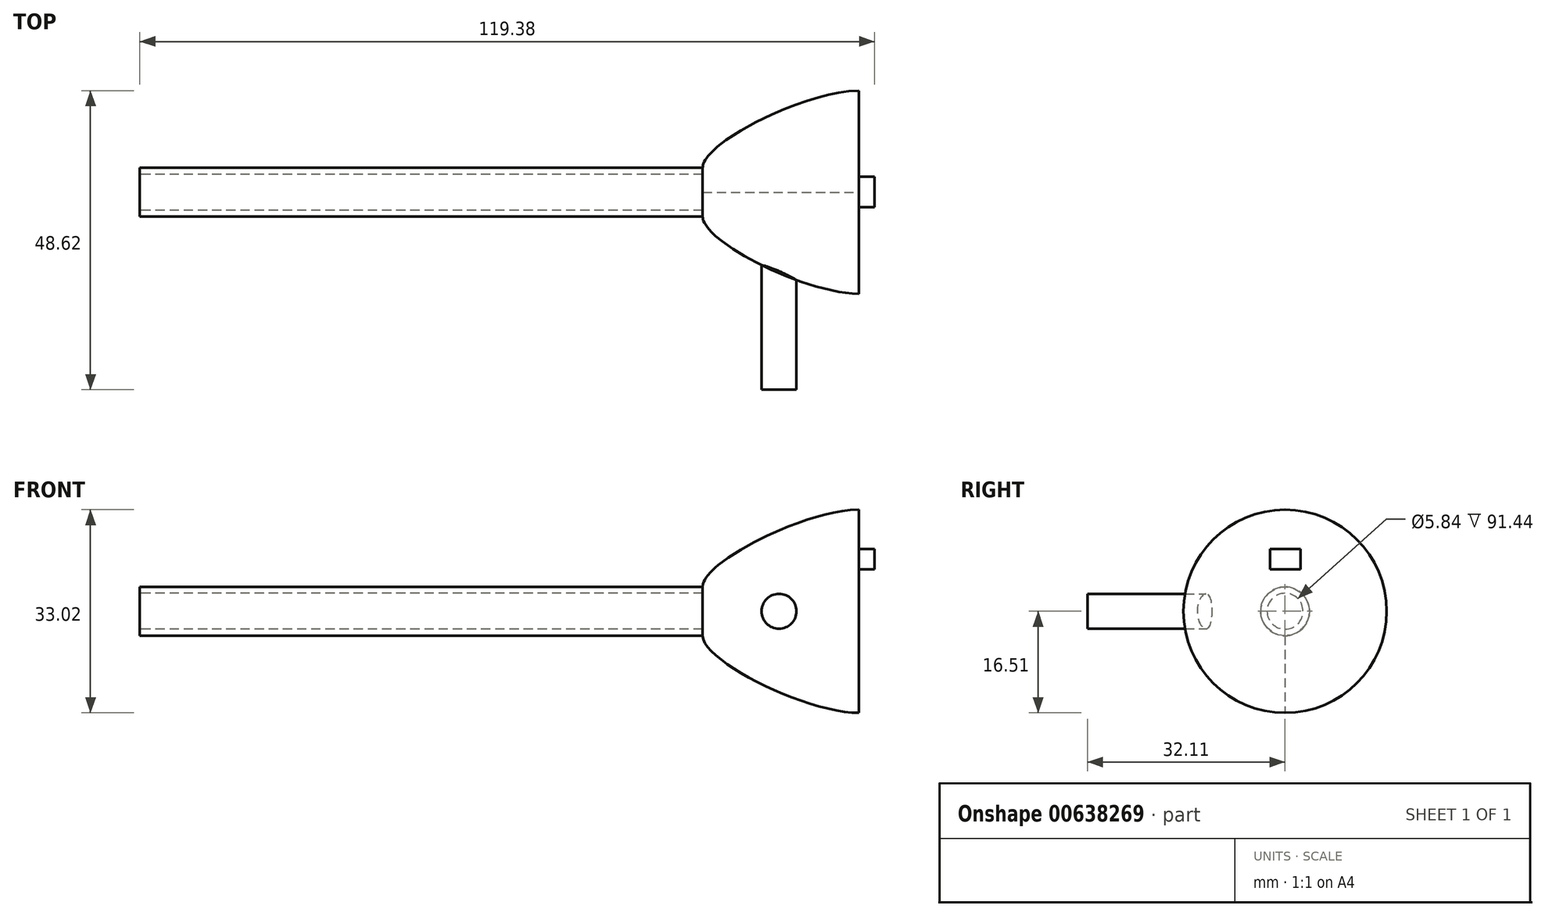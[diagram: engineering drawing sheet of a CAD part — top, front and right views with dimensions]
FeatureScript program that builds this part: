
annotation { "Feature Type Name" : "Feature", "Feature Type Description" : "" }
export const myFeature = defineFeature(function(context is Context, id is Id, definition is map)
    precondition{}
    {
        {
            var Q0;
            Q0=qCreatedBy(makeId("Right.planeOp"),FACE);
            var sketch = newSketch(context, id + "F0", { "sketchPlane" : qUnion([Q0])});
            skCircle(sketch, "E0", {"center": v(0, 0) * mm, "radius": 3.98 * mm});
            skCircle(sketch, "E1", {"center": v(0, 0) * mm, "radius": 2.92 * mm});
            skSolve(sketch);
        }
        {
            var Q0;
            Q0 = qSketchRegion(id + "F0", true);
            extrude(context, id + "F1", {"entities" : qUnion([Q0]), "depth" : 91.44 * mm, "offsetDistance" : 25.4 * mm});
        }
        {
            var Q0;
            Q0=makeQuery(id+"F1.opExtrude","CAP_FACE",FACE,{"disambiguationData":[OSD([sQuery(id+"F0.wireOp",EDGE,"E0"),sQuery(id+"F0.wireOp",EDGE,"E1")])],"isStart":false});
            cPlane(context, id + "F2", {"entities" : qUnion([Q0]), "cplaneType" : CPlaneType.OFFSET, "offset" : 25.4 * mm, "width" : 152.4 * mm, "height" : 152.4 * mm});
        }
        {
            var Q0;
            Q0=makeQuery(id+"F1.opExtrude","CAP_FACE",FACE,{"disambiguationData":[OSD([sQuery(id+"F0.wireOp",EDGE,"E0"),sQuery(id+"F0.wireOp",EDGE,"E1")])],"isStart":false});
            var sketch = newSketch(context, id + "F3", { "sketchPlane" : qUnion([Q0])});
            skCircle(sketch, "E2", {"center": v(0, 0) * mm, "radius": 3.98 * mm});
            skSolve(sketch);
        }
        {
            var Q0;
            Q0=qCreatedBy(id+"F2.planeOp",FACE);
            var sketch = newSketch(context, id + "F4", { "sketchPlane" : qUnion([Q0])});
            skCircle(sketch, "E3", {"center": v(0, 0) * mm, "radius": 16.51 * mm});
            skSolve(sketch);
        }
        {
            var Q1;
            Q1 = qSketchRegion(id + "F3", true);
            var Q2;
            Q2 = qSketchRegion(id + "F4", true);
            loft(context, id + "F5", {"operationType" : NewBodyOperationType.ADD, "startCondition" : LoftEndDerivativeType.TANGENT_TO_PROFILE, "startMagnitude" : 1, "endCondition" : LoftEndDerivativeType.NORMAL_TO_PROFILE, "endMagnitude" : 1, "sheetProfilesArray" : [{ "sheetProfileEntities" : qUnion([Q1]) }, { "sheetProfileEntities" : qUnion([Q2]) }]});
        }
        {
            var Q0;
            Q0=qCreatedBy(makeId("Front.planeOp"),FACE);
            var sketch = newSketch(context, id + "F6", { "sketchPlane" : qUnion([Q0])});
            skCircle(sketch, "E4", {"center": v(103.84, 0) * mm, "radius": 2.83 * mm});
            skLineSegment(sketch, "E5", {"start": v(91.44, -12.62) * mm, "end": v(91.44, 18.08) * mm, "construction": true});
            skSolve(sketch);
        }
        {
            var Q0;
            Q0 = qSketchRegion(id + "F6", true);
            extrude(context, id + "F7", {"entities" : qUnion([Q0]), "operationType" : NewBodyOperationType.ADD, "depth" : 32.1 * mm, "offsetDistance" : 25.4 * mm});
        }
        {
            var Q0;
            Q0=makeQuery(id+"F5.opLoft","CAP_FACE",FACE,{"disambiguationData":[OSD([makeQuery(id+"F4.imprint","IMPRINT",FACE,{"disambiguationData":[TD([[makeQuery(id+"F4.imprint","IMPRINT",EDGE,{"derivedFrom":sQuery(id+"F4.wireOp",EDGE,"E3")}),1.0]])]})])],"isStart":true});
            var sketch = newSketch(context, id + "F8", { "sketchPlane" : qUnion([Q0])});
            skLineSegment(sketch, "E6.bottom", {"start": v(2.54, 10.13) * mm, "end": v(-2.45, 10.13) * mm});
            skLineSegment(sketch, "E6.top", {"start": v(2.54, 6.83) * mm, "end": v(-2.45, 6.83) * mm});
            skLineSegment(sketch, "E6.left", {"start": v(2.54, 10.13) * mm, "end": v(2.54, 6.83) * mm});
            skLineSegment(sketch, "E6.right", {"start": v(-2.45, 10.13) * mm, "end": v(-2.45, 6.83) * mm});
            skSolve(sketch);
        }
        {
            var Q0;
            Q0 = qSketchRegion(id + "F8", true);
            extrude(context, id + "F9", {"entities" : qUnion([Q0]), "operationType" : NewBodyOperationType.ADD, "depth" : 2.54 * mm, "offsetDistance" : 25.4 * mm});
        }
    });
